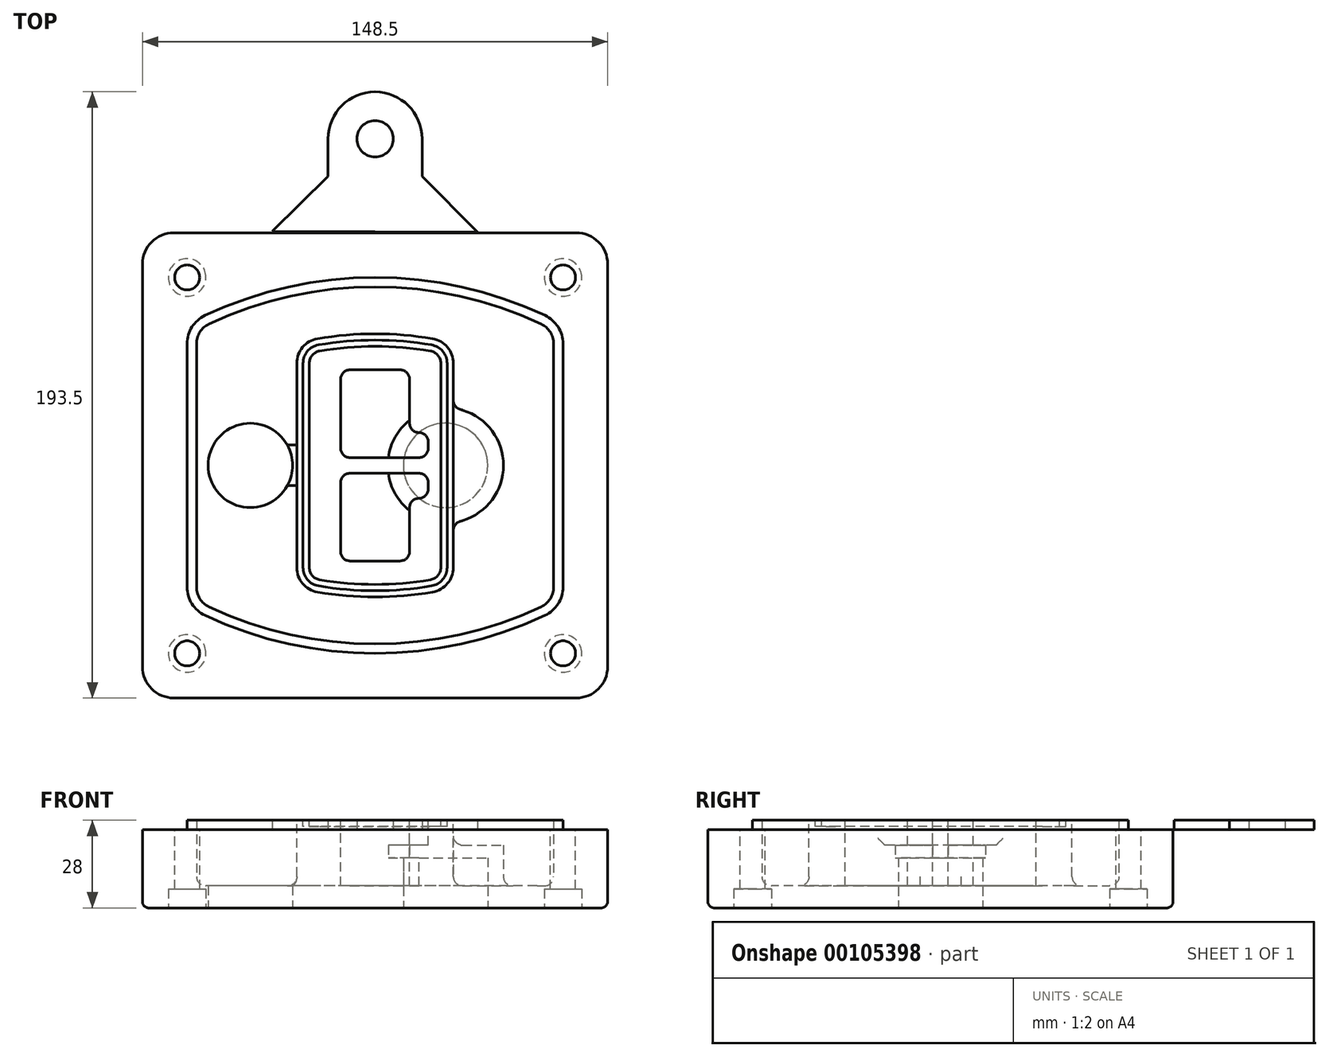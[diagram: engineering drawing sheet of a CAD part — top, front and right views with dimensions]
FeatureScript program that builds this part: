
annotation { "Feature Type Name" : "Feature", "Feature Type Description" : "" }
export const myFeature = defineFeature(function(context is Context, id is Id, definition is map)
    precondition{}
    {
        {
            var Q0;
            Q0=qCreatedBy(makeId("Top.planeOp"),FACE);
            var sketch = newSketch(context, id + "F0", { "sketchPlane" : qUnion([Q0])});
            skPoint(sketch, "E0.rect.middle", {"position": v(0, 0) * mm});
            skLineSegment(sketch, "E1.bottom", {"start": v(-64.25, -74.25) * mm, "end": v(64.25, -74.25) * mm});
            skLineSegment(sketch, "E1.top", {"start": v(-64.25, 74.25) * mm, "end": v(64.25, 74.25) * mm});
            skLineSegment(sketch, "E1.left", {"start": v(-74.25, -64.25) * mm, "end": v(-74.25, 64.25) * mm});
            skLineSegment(sketch, "E1.right", {"start": v(74.25, -64.25) * mm, "end": v(74.25, 64.25) * mm});
            skLineSegment(sketch, "E2", {"start": v(-74.25, 74.25) * mm, "end": v(74.25, -74.25) * mm, "construction": true});
            skLineSegment(sketch, "E3", {"start": v(74.25, 74.25) * mm, "end": v(-74.25, -74.25) * mm, "construction": true});
            skCircle(sketch, "E4", {"center": v(-60, 60) * mm, "radius": 4 * mm});
            skCircle(sketch, "E5", {"center": v(60, 60) * mm, "radius": 4 * mm});
            skCircle(sketch, "E6", {"center": v(60, -60) * mm, "radius": 4 * mm});
            skCircle(sketch, "E7", {"center": v(-60, -60) * mm, "radius": 4 * mm});
            skLineSegment(sketch, "E8", {"start": v(-60, 60) * mm, "end": v(60, 60) * mm, "construction": true});
            skLineSegment(sketch, "E9", {"start": v(60, 60) * mm, "end": v(60, -60) * mm, "construction": true});
            skLineSegment(sketch, "E10", {"start": v(60, -60) * mm, "end": v(-60, -60) * mm, "construction": true});
            skLineSegment(sketch, "E11", {"start": v(-60, -60) * mm, "end": v(-60, 60) * mm, "construction": true});
            skLineSegment(sketch, "E12", {"start": v(-60, 38.83) * mm, "end": v(-60, -38.83) * mm});
            skLineSegment(sketch, "E13", {"start": v(60, 38.83) * mm, "end": v(60, -38.83) * mm});
            skArc(sketch, "E14", {"start": v(54.26, 47.88) * mm, "mid": v(0, 60) * mm, "end": v(-54.26, 47.88) * mm});
            skArc(sketch, "E15", {"start": v(-54.26, -47.88) * mm, "mid": v(0, -60) * mm, "end": v(54.26, -47.88) * mm});
            skLineSegment(sketch, "E16", {"start": v(-60, 0) * mm, "end": v(60, 0) * mm, "construction": true});
            skPoint(sketch, "E17.visualSharp", {"position": v(-60, -45) * mm});
            skArc(sketch, "E17.filletArc", {"start": v(-60, -38.83) * mm, "mid": v(-58.44, -44.2) * mm, "end": v(-54.26, -47.88) * mm});
            skPoint(sketch, "E18.visualSharp", {"position": v(-60, 45) * mm});
            skArc(sketch, "E18.filletArc", {"start": v(-54.26, 47.88) * mm, "mid": v(-58.44, 44.2) * mm, "end": v(-60, 38.83) * mm});
            skPoint(sketch, "E19.visualSharp", {"position": v(60, 45) * mm});
            skArc(sketch, "E19.filletArc", {"start": v(60, 38.83) * mm, "mid": v(58.44, 44.2) * mm, "end": v(54.26, 47.88) * mm});
            skPoint(sketch, "E20.visualSharp", {"position": v(60, -45) * mm});
            skArc(sketch, "E20.filletArc", {"start": v(54.26, -47.88) * mm, "mid": v(58.44, -44.2) * mm, "end": v(60, -38.83) * mm});
            skPoint(sketch, "E21.visualSharp", {"position": v(-74.25, 74.25) * mm});
            skArc(sketch, "E21.filletArc", {"start": v(-64.25, 74.25) * mm, "mid": v(-71.32, 71.32) * mm, "end": v(-74.25, 64.25) * mm});
            skPoint(sketch, "E22.visualSharp", {"position": v(74.25, 74.25) * mm});
            skArc(sketch, "E22.filletArc", {"start": v(74.25, 64.25) * mm, "mid": v(71.32, 71.32) * mm, "end": v(64.25, 74.25) * mm});
            skPoint(sketch, "E23.visualSharp", {"position": v(74.25, -74.25) * mm});
            skArc(sketch, "E23.filletArc", {"start": v(64.25, -74.25) * mm, "mid": v(71.32, -71.32) * mm, "end": v(74.25, -64.25) * mm});
            skPoint(sketch, "E24.visualSharp", {"position": v(-74.25, -74.25) * mm});
            skArc(sketch, "E24.filletArc", {"start": v(-74.25, -64.25) * mm, "mid": v(-71.32, -71.32) * mm, "end": v(-64.25, -74.25) * mm});
            skArc(sketch, "E25.0", {"start": v(57, 38.83) * mm, "mid": v(55.9, 42.58) * mm, "end": v(52.98, 45.17) * mm});
            skLineSegment(sketch, "E25.1", {"start": v(57, 38.83) * mm, "end": v(57, -38.83) * mm});
            skArc(sketch, "E25.2", {"start": v(52.98, -45.17) * mm, "mid": v(55.9, -42.58) * mm, "end": v(57, -38.83) * mm});
            skArc(sketch, "E25.3", {"start": v(-52.98, -45.17) * mm, "mid": v(0, -57) * mm, "end": v(52.98, -45.17) * mm});
            skArc(sketch, "E25.4", {"start": v(-57, -38.83) * mm, "mid": v(-55.9, -42.58) * mm, "end": v(-52.98, -45.17) * mm});
            skArc(sketch, "E25.5", {"start": v(52.98, 45.17) * mm, "mid": v(0, 57) * mm, "end": v(-52.98, 45.17) * mm});
            skLineSegment(sketch, "E25.6", {"start": v(-57, 38.83) * mm, "end": v(-57, -38.83) * mm});
            skArc(sketch, "E25.7", {"start": v(-52.98, 45.17) * mm, "mid": v(-55.9, 42.58) * mm, "end": v(-57, 38.83) * mm});
            skArc(sketch, "E26.0", {"start": v(-55.96, 51.5) * mm, "mid": v(-61.82, 46.33) * mm, "end": v(-64, 38.83) * mm});
            skArc(sketch, "E26.1", {"start": v(55.96, 51.5) * mm, "mid": v(0, 64) * mm, "end": v(-55.96, 51.5) * mm});
            skArc(sketch, "E26.2", {"start": v(64, 38.83) * mm, "mid": v(61.82, 46.33) * mm, "end": v(55.96, 51.5) * mm});
            skLineSegment(sketch, "E26.3", {"start": v(64, 38.83) * mm, "end": v(64, -38.83) * mm});
            skArc(sketch, "E26.4", {"start": v(55.96, -51.5) * mm, "mid": v(61.82, -46.33) * mm, "end": v(64, -38.83) * mm});
            skLineSegment(sketch, "E26.5", {"start": v(-64, 38.83) * mm, "end": v(-64, -38.83) * mm});
            skArc(sketch, "E26.6", {"start": v(-55.96, -51.5) * mm, "mid": v(0, -64) * mm, "end": v(55.96, -51.5) * mm});
            skArc(sketch, "E26.7", {"start": v(-64, -38.83) * mm, "mid": v(-61.82, -46.33) * mm, "end": v(-55.96, -51.5) * mm});
            skSolve(sketch);
        }
        {
            var Q0;
            Q0=makeQuery(id+"F0.imprint","IMPRINT",FACE,{"disambiguationData":[TD([[makeQuery(id+"F0.imprint","IMPRINT",EDGE,{"derivedFrom":sQuery(id+"F0.wireOp",EDGE,"E1.bottom")}),1.0]])]});
            var Q1;
            Q1=makeQuery(id+"F0.imprint","IMPRINT",FACE,{"disambiguationData":[TD([[makeQuery(id+"F0.imprint","IMPRINT",EDGE,{"derivedFrom":sQuery(id+"F0.wireOp",EDGE,"E12")}),1.0]])]});
            var Q2;
            Q2=makeQuery(id+"F0.imprint","IMPRINT",FACE,{"disambiguationData":[TD([[makeQuery(id+"F0.imprint","IMPRINT",EDGE,{"derivedFrom":sQuery(id+"F0.wireOp",EDGE,"E25.0")}),1.0]])]});
            var Q3;
            Q3=makeQuery(id+"F0.imprint","IMPRINT",FACE,{"disambiguationData":[TD([[makeQuery(id+"F0.imprint","IMPRINT",EDGE,{"derivedFrom":sQuery(id+"F0.wireOp",EDGE,"E12")}),-1.0]])]});
            extrude(context, id + "F1", {"entities" : qUnion([Q0, Q1, Q2, Q3]), "oppositeDirection" : true, "depth" : 25 * mm});
        }
        {
            var Q0;
            Q0=makeQuery(id+"F0.imprint","IMPRINT",FACE,{"disambiguationData":[TD([[makeQuery(id+"F0.imprint","IMPRINT",EDGE,{"derivedFrom":sQuery(id+"F0.wireOp",EDGE,"E12")}),1.0]])]});
            extrude(context, id + "F2", {"entities" : qUnion([Q0]), "operationType" : NewBodyOperationType.ADD, "depth" : 3 * mm});
        }
        {
            var Q0;
            Q0=makeQuery(id+"F0.imprint","IMPRINT",FACE,{"disambiguationData":[TD([[makeQuery(id+"F0.imprint","IMPRINT",EDGE,{"derivedFrom":sQuery(id+"F0.wireOp",EDGE,"E25.0")}),1.0]])]});
            extrude(context, id + "F3", {"entities" : qUnion([Q0]), "operationType" : NewBodyOperationType.REMOVE, "oppositeDirection" : true, "depth" : 18 * mm});
        }
        {
            var Q0;
            Q0=makeQuery(id+"F2.opExtrude","CAP_FACE",FACE,{"disambiguationData":[OSD([sQuery(id+"F0.wireOp",EDGE,"E12"),sQuery(id+"F0.wireOp",EDGE,"E13"),sQuery(id+"F0.wireOp",EDGE,"E14"),sQuery(id+"F0.wireOp",EDGE,"E15"),sQuery(id+"F0.wireOp",EDGE,"E17.filletArc"),sQuery(id+"F0.wireOp",EDGE,"E18.filletArc"),sQuery(id+"F0.wireOp",EDGE,"E19.filletArc"),sQuery(id+"F0.wireOp",EDGE,"E20.filletArc"),sQuery(id+"F0.wireOp",EDGE,"E25.0"),sQuery(id+"F0.wireOp",EDGE,"E25.1"),sQuery(id+"F0.wireOp",EDGE,"E25.2"),sQuery(id+"F0.wireOp",EDGE,"E25.3"),sQuery(id+"F0.wireOp",EDGE,"E25.4"),sQuery(id+"F0.wireOp",EDGE,"E25.5"),sQuery(id+"F0.wireOp",EDGE,"E25.6"),sQuery(id+"F0.wireOp",EDGE,"E25.7")])],"isStart":false});
            var sketch = newSketch(context, id + "F4", { "sketchPlane" : qUnion([Q0])});
            skArc(sketch, "E27.0", {"start": v(-18.34, -40.45) * mm, "mid": v(0, -42) * mm, "end": v(18.34, -40.45) * mm});
            skArc(sketch, "E28.0", {"start": v(18.34, 40.45) * mm, "mid": v(0, 42) * mm, "end": v(-18.34, 40.45) * mm});
            skLineSegment(sketch, "E29", {"start": v(-25, 32.57) * mm, "end": v(-25, -32.57) * mm});
            skLineSegment(sketch, "E30", {"start": v(25, 32.57) * mm, "end": v(25, -32.57) * mm});
            skLineSegment(sketch, "E31", {"start": v(-25, 39.1) * mm, "end": v(25, 39.1) * mm, "construction": true});
            skLineSegment(sketch, "E32", {"start": v(-25, -39.1) * mm, "end": v(25, -39.1) * mm, "construction": true});
            skPoint(sketch, "E33.visualSharp", {"position": v(-25, 39.1) * mm});
            skArc(sketch, "E33.filletArc", {"start": v(-18.34, 40.45) * mm, "mid": v(-23.11, 37.73) * mm, "end": v(-25, 32.57) * mm});
            skPoint(sketch, "E34.visualSharp", {"position": v(25, 39.1) * mm});
            skArc(sketch, "E34.filletArc", {"start": v(25, 32.57) * mm, "mid": v(23.11, 37.73) * mm, "end": v(18.34, 40.45) * mm});
            skPoint(sketch, "E35.visualSharp", {"position": v(25, -39.1) * mm});
            skArc(sketch, "E35.filletArc", {"start": v(18.34, -40.45) * mm, "mid": v(23.11, -37.73) * mm, "end": v(25, -32.57) * mm});
            skPoint(sketch, "E36.visualSharp", {"position": v(-25, -39.1) * mm});
            skArc(sketch, "E36.filletArc", {"start": v(-25, -32.57) * mm, "mid": v(-23.11, -37.73) * mm, "end": v(-18.34, -40.45) * mm});
            skArc(sketch, "E37.0", {"start": v(52.98, 45.17) * mm, "mid": v(0, 57) * mm, "end": v(-52.98, 45.17) * mm});
            skArc(sketch, "E37.1", {"start": v(-52.98, 45.17) * mm, "mid": v(-55.9, 42.58) * mm, "end": v(-57, 38.83) * mm});
            skLineSegment(sketch, "E37.2", {"start": v(-57, 38.83) * mm, "end": v(-57, -38.83) * mm});
            skArc(sketch, "E37.3", {"start": v(-57, -38.83) * mm, "mid": v(-55.9, -42.58) * mm, "end": v(-52.98, -45.17) * mm});
            skArc(sketch, "E37.4", {"start": v(-52.98, -45.17) * mm, "mid": v(0, -57) * mm, "end": v(52.98, -45.17) * mm});
            skArc(sketch, "E37.5", {"start": v(52.98, -45.17) * mm, "mid": v(55.9, -42.58) * mm, "end": v(57, -38.83) * mm});
            skLineSegment(sketch, "E37.6", {"start": v(57, 38.83) * mm, "end": v(57, -38.83) * mm});
            skArc(sketch, "E37.7", {"start": v(57, 38.83) * mm, "mid": v(55.9, 42.58) * mm, "end": v(52.98, 45.17) * mm});
            skLineSegment(sketch, "E38.0", {"start": v(23, 32.57) * mm, "end": v(23, -32.57) * mm});
            skArc(sketch, "E38.1", {"start": v(18, -38.48) * mm, "mid": v(21.58, -36.44) * mm, "end": v(23, -32.57) * mm});
            skArc(sketch, "E38.2", {"start": v(-18, -38.48) * mm, "mid": v(0, -40) * mm, "end": v(18, -38.48) * mm});
            skArc(sketch, "E38.3", {"start": v(-23, -32.57) * mm, "mid": v(-21.58, -36.44) * mm, "end": v(-18, -38.48) * mm});
            skLineSegment(sketch, "E38.4", {"start": v(-23, 32.57) * mm, "end": v(-23, -32.57) * mm});
            skArc(sketch, "E38.5", {"start": v(23, 32.57) * mm, "mid": v(21.58, 36.44) * mm, "end": v(18, 38.48) * mm});
            skArc(sketch, "E38.6", {"start": v(-18, 38.48) * mm, "mid": v(-21.58, 36.44) * mm, "end": v(-23, 32.57) * mm});
            skArc(sketch, "E38.7", {"start": v(18, 38.48) * mm, "mid": v(0, 40) * mm, "end": v(-18, 38.48) * mm});
            skArc(sketch, "E39.0", {"start": v(21, 32.57) * mm, "mid": v(20.06, 35.15) * mm, "end": v(17.67, 36.5) * mm});
            skLineSegment(sketch, "E39.1", {"start": v(21, 32.57) * mm, "end": v(21, -32.57) * mm});
            skArc(sketch, "E39.2", {"start": v(17.67, -36.5) * mm, "mid": v(20.06, -35.15) * mm, "end": v(21, -32.57) * mm});
            skArc(sketch, "E39.3", {"start": v(-17.67, -36.5) * mm, "mid": v(0, -38) * mm, "end": v(17.67, -36.5) * mm});
            skArc(sketch, "E39.4", {"start": v(-21, -32.57) * mm, "mid": v(-20.06, -35.15) * mm, "end": v(-17.67, -36.5) * mm});
            skArc(sketch, "E39.5", {"start": v(17.67, 36.5) * mm, "mid": v(0, 38) * mm, "end": v(-17.67, 36.5) * mm});
            skLineSegment(sketch, "E39.6", {"start": v(-21, 32.57) * mm, "end": v(-21, -32.57) * mm});
            skArc(sketch, "E39.7", {"start": v(-17.67, 36.5) * mm, "mid": v(-20.06, 35.15) * mm, "end": v(-21, 32.57) * mm});
            skLineSegment(sketch, "E40", {"start": v(-25, 0) * mm, "end": v(25, 0) * mm, "construction": true});
            skLineSegment(sketch, "E41", {"start": v(-11, 5.5) * mm, "end": v(-11, 27.5) * mm});
            skLineSegment(sketch, "E42", {"start": v(-8, 30.5) * mm, "end": v(8, 30.5) * mm});
            skLineSegment(sketch, "E43", {"start": v(11, 27.5) * mm, "end": v(11, 13.5) * mm});
            skLineSegment(sketch, "E44", {"start": v(14, 10.5) * mm, "end": v(14, 10.5) * mm});
            skLineSegment(sketch, "E45", {"start": v(17, 7.5) * mm, "end": v(17, 5.5) * mm});
            skLineSegment(sketch, "E46", {"start": v(14, 2.5) * mm, "end": v(-8, 2.5) * mm});
            skPoint(sketch, "E47.visualSharp", {"position": v(-11, 30.5) * mm});
            skArc(sketch, "E47.filletArc", {"start": v(-8, 30.5) * mm, "mid": v(-10.12, 29.62) * mm, "end": v(-11, 27.5) * mm});
            skPoint(sketch, "E48.visualSharp", {"position": v(11, 30.5) * mm});
            skArc(sketch, "E48.filletArc", {"start": v(11, 27.5) * mm, "mid": v(10.12, 29.62) * mm, "end": v(8, 30.5) * mm});
            skPoint(sketch, "E49.visualSharp", {"position": v(11, 10.5) * mm});
            skArc(sketch, "E49.filletArc", {"start": v(11, 13.5) * mm, "mid": v(11.88, 11.38) * mm, "end": v(14, 10.5) * mm});
            skPoint(sketch, "E50.visualSharp", {"position": v(17, 10.5) * mm});
            skArc(sketch, "E50.filletArc", {"start": v(17, 7.5) * mm, "mid": v(16.12, 9.62) * mm, "end": v(14, 10.5) * mm});
            skPoint(sketch, "E51.visualSharp", {"position": v(17, 2.5) * mm});
            skArc(sketch, "E51.filletArc", {"start": v(14, 2.5) * mm, "mid": v(16.12, 3.38) * mm, "end": v(17, 5.5) * mm});
            skPoint(sketch, "E52.visualSharp", {"position": v(-11, 2.5) * mm});
            skArc(sketch, "E52.filletArc", {"start": v(-11, 5.5) * mm, "mid": v(-10.12, 3.38) * mm, "end": v(-8, 2.5) * mm});
            skLineSegment(sketch, "E53.0.MirrorCS", {"start": v(14, -2.5) * mm, "end": v(-8, -2.5) * mm});
            skArc(sketch, "E54.0.MirrorCS", {"start": v(-11, -5.5) * mm, "mid": v(-10.12, -3.38) * mm, "end": v(-8, -2.5) * mm});
            skLineSegment(sketch, "E55.0.MirrorCS", {"start": v(-11, -5.5) * mm, "end": v(-11, -27.5) * mm});
            skArc(sketch, "E56.0.MirrorCS", {"start": v(-8, -30.5) * mm, "mid": v(-10.12, -29.62) * mm, "end": v(-11, -27.5) * mm});
            skLineSegment(sketch, "E57.0.MirrorCS", {"start": v(-8, -30.5) * mm, "end": v(8, -30.5) * mm});
            skArc(sketch, "E58.0.MirrorCS", {"start": v(11, -27.5) * mm, "mid": v(10.12, -29.62) * mm, "end": v(8, -30.5) * mm});
            skLineSegment(sketch, "E59.0.MirrorCS", {"start": v(11, -27.5) * mm, "end": v(11, -13.5) * mm});
            skArc(sketch, "E60.0.MirrorCS", {"start": v(11, -13.5) * mm, "mid": v(11.88, -11.38) * mm, "end": v(14, -10.5) * mm});
            skArc(sketch, "E61.0.MirrorCS", {"start": v(17, -7.5) * mm, "mid": v(16.12, -9.62) * mm, "end": v(14, -10.5) * mm});
            skLineSegment(sketch, "E62.0.MirrorCS", {"start": v(17, -7.5) * mm, "end": v(17, -5.5) * mm});
            skArc(sketch, "E63.0.MirrorCS", {"start": v(14, -2.5) * mm, "mid": v(16.12, -3.38) * mm, "end": v(17, -5.5) * mm});
            skSolve(sketch);
        }
        {
            var Q0;
            Q0=makeQuery(id+"F4.imprint","IMPRINT",FACE,{"disambiguationData":[TD([[makeQuery(id+"F4.imprint","IMPRINT",EDGE,{"derivedFrom":sQuery(id+"F4.wireOp",EDGE,"E27.0")}),1.0]])]});
            var Q1;
            Q1=makeQuery(id+"F4.imprint","IMPRINT",FACE,{"disambiguationData":[TD([[makeQuery(id+"F4.imprint","IMPRINT",EDGE,{"derivedFrom":sQuery(id+"F4.wireOp",EDGE,"E38.0")}),-1.0]])]});
            var Q2;
            Q2=makeQuery(id+"F4.imprint","IMPRINT",FACE,{"disambiguationData":[TD([[makeQuery(id+"F4.imprint","IMPRINT",EDGE,{"derivedFrom":sQuery(id+"F4.wireOp",EDGE,"E39.0")}),1.0]])]});
            extrude(context, id + "F5", {"entities" : qUnion([Q0, Q1, Q2]), "operationType" : NewBodyOperationType.ADD, "endBound" : BoundingType.UP_TO_NEXT, "oppositeDirection" : true, "depth" : 25 * mm});
        }
        {
            var Q0;
            Q0=makeQuery(id+"F4.imprint","IMPRINT",FACE,{"disambiguationData":[TD([[makeQuery(id+"F4.imprint","IMPRINT",EDGE,{"derivedFrom":sQuery(id+"F4.wireOp",EDGE,"E38.0")}),-1.0]])]});
            extrude(context, id + "F6", {"entities" : qUnion([Q0]), "operationType" : NewBodyOperationType.REMOVE, "oppositeDirection" : true, "depth" : 2 * mm});
        }
        {
            var Q0;
            Q0=makeQuery(id+"F1.opExtrude","CAP_FACE",FACE,{"disambiguationData":[OSD([sQuery(id+"F0.wireOp",EDGE,"E1.bottom"),sQuery(id+"F0.wireOp",EDGE,"E1.top"),sQuery(id+"F0.wireOp",EDGE,"E1.left"),sQuery(id+"F0.wireOp",EDGE,"E1.right"),sQuery(id+"F0.wireOp",EDGE,"E4"),sQuery(id+"F0.wireOp",EDGE,"E5"),sQuery(id+"F0.wireOp",EDGE,"E6"),sQuery(id+"F0.wireOp",EDGE,"E7"),sQuery(id+"F0.wireOp",EDGE,"E21.filletArc"),sQuery(id+"F0.wireOp",EDGE,"E22.filletArc"),sQuery(id+"F0.wireOp",EDGE,"E23.filletArc"),sQuery(id+"F0.wireOp",EDGE,"E24.filletArc")])],"isStart":false});
            var sketch = newSketch(context, id + "F7", { "sketchPlane" : qUnion([Q0])});
            skCircle(sketch, "E64", {"center": v(22.5, 0) * mm, "radius": 13.47 * mm});
            skCircle(sketch, "E65", {"center": v(-39.81, 0) * mm, "radius": 13.47 * mm});
            skLineSegment(sketch, "E66", {"start": v(74.25, 0) * mm, "end": v(-74.25, 0) * mm});
            skCircle(sketch, "E67", {"center": v(22.5, 0) * mm, "radius": 18.47 * mm});
            skCircle(sketch, "E68", {"center": v(60, -60) * mm, "radius": 6 * mm});
            skCircle(sketch, "E69", {"center": v(-60, -60) * mm, "radius": 6 * mm});
            skCircle(sketch, "E70", {"center": v(-60, 60) * mm, "radius": 6 * mm});
            skCircle(sketch, "E71", {"center": v(60, 60) * mm, "radius": 6 * mm});
            skSolve(sketch);
        }
        {
            var Q0;
            {var subQ1=sQuery(id+"F7.wireOp",EDGE,"E66");var subQ4=sQuery(id+"F7.wireOp",EDGE,"E64");var subQ6=makeQuery(id+"F7.imprint","INTERSECT",VERTEX,{"disambiguationData":[OD(0.0)],"derivedFrom":[subQ4,subQ1]});Q0=makeQuery(id+"F7.imprint","IMPRINT",FACE,{"disambiguationData":[TD([[makeQuery(id+"F7.imprint","IMPRINT",EDGE,{"disambiguationData":[TD([[subQ6,-1.0]])],"derivedFrom":subQ4}),-1.0]])]});}
            var Q1;
            {var subQ0=sQuery(id+"F7.wireOp",EDGE,"E66");var subQ1=sQuery(id+"F7.wireOp",EDGE,"E64");var subQ3=makeQuery(id+"F7.imprint","INTERSECT",VERTEX,{"disambiguationData":[OD(0.0)],"derivedFrom":[subQ1,subQ0]});Q1=makeQuery(id+"F7.imprint","IMPRINT",FACE,{"disambiguationData":[TD([[makeQuery(id+"F7.imprint","IMPRINT",EDGE,{"disambiguationData":[TD([[subQ3,-1.0]])],"derivedFrom":subQ1}),1.0]])]});}
            var Q2;
            {var subQ0=sQuery(id+"F7.wireOp",EDGE,"E66");var subQ1=sQuery(id+"F7.wireOp",EDGE,"E64");var subQ3=makeQuery(id+"F7.imprint","INTERSECT",VERTEX,{"disambiguationData":[OD(0.0)],"derivedFrom":[subQ1,subQ0]});Q2=makeQuery(id+"F7.imprint","IMPRINT",FACE,{"disambiguationData":[TD([[makeQuery(id+"F7.imprint","IMPRINT",EDGE,{"disambiguationData":[TD([[subQ3,1.0]])],"derivedFrom":subQ1}),1.0]])]});}
            var Q3;
            {var subQ1=sQuery(id+"F7.wireOp",EDGE,"E66");var subQ4=sQuery(id+"F7.wireOp",EDGE,"E64");var subQ6=makeQuery(id+"F7.imprint","INTERSECT",VERTEX,{"disambiguationData":[OD(0.0)],"derivedFrom":[subQ4,subQ1]});Q3=makeQuery(id+"F7.imprint","IMPRINT",FACE,{"disambiguationData":[TD([[makeQuery(id+"F7.imprint","IMPRINT",EDGE,{"disambiguationData":[TD([[subQ6,1.0]])],"derivedFrom":subQ4}),-1.0]])]});}
            extrude(context, id + "F8", {"entities" : qUnion([Q0, Q1, Q2, Q3]), "operationType" : NewBodyOperationType.ADD, "oppositeDirection" : true, "depth" : 20 * mm});
        }
        {
            var Q0;
            {var subQ0=sQuery(id+"F7.wireOp",EDGE,"E66");var subQ1=sQuery(id+"F7.wireOp",EDGE,"E64");var subQ3=makeQuery(id+"F7.imprint","INTERSECT",VERTEX,{"disambiguationData":[OD(0.0)],"derivedFrom":[subQ1,subQ0]});Q0=makeQuery(id+"F7.imprint","IMPRINT",FACE,{"disambiguationData":[TD([[makeQuery(id+"F7.imprint","IMPRINT",EDGE,{"disambiguationData":[TD([[subQ3,-1.0]])],"derivedFrom":subQ1}),1.0]])]});}
            var Q1;
            {var subQ0=sQuery(id+"F7.wireOp",EDGE,"E66");var subQ1=sQuery(id+"F7.wireOp",EDGE,"E64");var subQ3=makeQuery(id+"F7.imprint","INTERSECT",VERTEX,{"disambiguationData":[OD(0.0)],"derivedFrom":[subQ1,subQ0]});Q1=makeQuery(id+"F7.imprint","IMPRINT",FACE,{"disambiguationData":[TD([[makeQuery(id+"F7.imprint","IMPRINT",EDGE,{"disambiguationData":[TD([[subQ3,1.0]])],"derivedFrom":subQ1}),1.0]])]});}
            extrude(context, id + "F9", {"entities" : qUnion([Q0, Q1]), "operationType" : NewBodyOperationType.REMOVE, "oppositeDirection" : true, "depth" : 16 * mm});
        }
        {
            var Q0;
            {var subQ0=sQuery(id+"F7.wireOp",EDGE,"E66");var subQ1=sQuery(id+"F7.wireOp",EDGE,"E65");var subQ3=makeQuery(id+"F7.imprint","INTERSECT",VERTEX,{"disambiguationData":[OD(0.0)],"derivedFrom":[subQ1,subQ0]});Q0=makeQuery(id+"F7.imprint","IMPRINT",FACE,{"disambiguationData":[TD([[makeQuery(id+"F7.imprint","IMPRINT",EDGE,{"disambiguationData":[TD([[subQ3,-1.0]])],"derivedFrom":subQ1}),1.0]])]});}
            var Q1;
            {var subQ0=sQuery(id+"F7.wireOp",EDGE,"E66");var subQ1=sQuery(id+"F7.wireOp",EDGE,"E65");var subQ3=makeQuery(id+"F7.imprint","INTERSECT",VERTEX,{"disambiguationData":[OD(0.0)],"derivedFrom":[subQ1,subQ0]});Q1=makeQuery(id+"F7.imprint","IMPRINT",FACE,{"disambiguationData":[TD([[makeQuery(id+"F7.imprint","IMPRINT",EDGE,{"disambiguationData":[TD([[subQ3,1.0]])],"derivedFrom":subQ1}),1.0]])]});}
            extrude(context, id + "F10", {"entities" : qUnion([Q0, Q1]), "operationType" : NewBodyOperationType.REMOVE, "oppositeDirection" : true, "depth" : 25 * mm});
        }
        {
            var Q0;
            Q0=makeQuery(id+"F7.imprint","IMPRINT",FACE,{"disambiguationData":[TD([[makeQuery(id+"F7.imprint","IMPRINT",EDGE,{"derivedFrom":sQuery(id+"F7.wireOp",EDGE,"E68")}),1.0]])]});
            var Q1;
            Q1=makeQuery(id+"F7.imprint","IMPRINT",FACE,{"disambiguationData":[TD([[makeQuery(id+"F7.imprint","IMPRINT",EDGE,{"derivedFrom":makeQuery(id+"F1.opExtrude","CAP_EDGE",EDGE,{"disambiguationData":[OSD([sQuery(id+"F0.wireOp",EDGE,"E5")])],"isStart":false})}),-1.0]])]});
            var Q2;
            Q2=makeQuery(id+"F7.imprint","IMPRINT",FACE,{"disambiguationData":[TD([[makeQuery(id+"F7.imprint","IMPRINT",EDGE,{"derivedFrom":sQuery(id+"F7.wireOp",EDGE,"E69")}),1.0]])]});
            var Q3;
            Q3=makeQuery(id+"F7.imprint","IMPRINT",FACE,{"disambiguationData":[TD([[makeQuery(id+"F7.imprint","IMPRINT",EDGE,{"derivedFrom":makeQuery(id+"F1.opExtrude","CAP_EDGE",EDGE,{"disambiguationData":[OSD([sQuery(id+"F0.wireOp",EDGE,"E4")])],"isStart":false})}),-1.0]])]});
            var Q4;
            Q4=makeQuery(id+"F7.imprint","IMPRINT",FACE,{"disambiguationData":[TD([[makeQuery(id+"F7.imprint","IMPRINT",EDGE,{"derivedFrom":sQuery(id+"F7.wireOp",EDGE,"E70")}),1.0]])]});
            var Q5;
            Q5=makeQuery(id+"F7.imprint","IMPRINT",FACE,{"disambiguationData":[TD([[makeQuery(id+"F7.imprint","IMPRINT",EDGE,{"derivedFrom":makeQuery(id+"F1.opExtrude","CAP_EDGE",EDGE,{"disambiguationData":[OSD([sQuery(id+"F0.wireOp",EDGE,"E7")])],"isStart":false})}),-1.0]])]});
            var Q6;
            Q6=makeQuery(id+"F7.imprint","IMPRINT",FACE,{"disambiguationData":[TD([[makeQuery(id+"F7.imprint","IMPRINT",EDGE,{"derivedFrom":sQuery(id+"F7.wireOp",EDGE,"E71")}),1.0]])]});
            var Q7;
            Q7=makeQuery(id+"F7.imprint","IMPRINT",FACE,{"disambiguationData":[TD([[makeQuery(id+"F7.imprint","IMPRINT",EDGE,{"derivedFrom":makeQuery(id+"F1.opExtrude","CAP_EDGE",EDGE,{"disambiguationData":[OSD([sQuery(id+"F0.wireOp",EDGE,"E6")])],"isStart":false})}),-1.0]])]});
            extrude(context, id + "F11", {"entities" : qUnion([Q0, Q1, Q2, Q3, Q4, Q5, Q6, Q7]), "operationType" : NewBodyOperationType.REMOVE, "oppositeDirection" : true, "depth" : 6 * mm});
        }
        {
            var Q0;
            Q0=makeQuery(id+"F9.boolean.opBoolean","COPY",FACE,{"derivedFrom":makeQuery(id+"F9.opExtrude","CAP_FACE",FACE,{"disambiguationData":[OSD([sQuery(id+"F7.wireOp",EDGE,"E64")])],"isStart":false})});
            var sketch = newSketch(context, id + "F12", { "sketchPlane" : qUnion([Q0])});
            skArc(sketch, "E72.0", {"start": v(11, 14.45) * mm, "mid": v(6.45, 9.13) * mm, "end": v(4.2, 2.5) * mm});
            skArc(sketch, "E72.1", {"start": v(4.2, -2.5) * mm, "mid": v(6.45, -9.13) * mm, "end": v(11, -14.45) * mm});
            skLineSegment(sketch, "E73", {"start": v(4.2, -2.5) * mm, "end": v(14, -2.5) * mm});
            skLineSegment(sketch, "E74.0", {"start": v(14, 2.5) * mm, "end": v(4.2, 2.5) * mm});
            skArc(sketch, "E74.1", {"start": v(14, 2.5) * mm, "mid": v(16.12, 3.38) * mm, "end": v(17, 5.5) * mm});
            skLineSegment(sketch, "E74.2", {"start": v(17, 7.5) * mm, "end": v(17, 5.5) * mm});
            skArc(sketch, "E74.3", {"start": v(17, 7.5) * mm, "mid": v(16.12, 9.62) * mm, "end": v(14, 10.5) * mm});
            skArc(sketch, "E74.4", {"start": v(11, 13.5) * mm, "mid": v(11.88, 11.38) * mm, "end": v(14, 10.5) * mm});
            skLineSegment(sketch, "E74.5", {"start": v(11, 14.45) * mm, "end": v(11, 13.5) * mm});
            skLineSegment(sketch, "E74.7", {"start": v(14, -2.5) * mm, "end": v(4.2, -2.5) * mm});
            skArc(sketch, "E74.8", {"start": v(14, -2.5) * mm, "mid": v(16.12, -3.38) * mm, "end": v(17, -5.5) * mm});
            skLineSegment(sketch, "E74.9", {"start": v(17, -7.5) * mm, "end": v(17, -5.5) * mm});
            skArc(sketch, "E74.10", {"start": v(17, -7.5) * mm, "mid": v(16.12, -9.62) * mm, "end": v(14, -10.5) * mm});
            skArc(sketch, "E74.11", {"start": v(11, -13.5) * mm, "mid": v(11.88, -11.38) * mm, "end": v(14, -10.5) * mm});
            skLineSegment(sketch, "E74.12", {"start": v(11, -14.45) * mm, "end": v(11, -13.5) * mm});
            skPoint(sketch, "E75.orphan", {"position": v(11, -27.5) * mm});
            skPoint(sketch, "E76.orphan", {"position": v(-8, -2.5) * mm});
            skPoint(sketch, "E77.orphan", {"position": v(-8, 2.5) * mm});
            skPoint(sketch, "E78.orphan", {"position": v(11, 27.5) * mm});
            skSolve(sketch);
        }
        {
            var Q0;
            {var subQ7=sQuery(id+"F12.wireOp",EDGE,"E72.0");var subQ14=sQuery(id+"F12.wireOp",EDGE,"E72.1");var subQ16=sQuery(id+"F12.wireOp",EDGE,"E74.1");var subQ18=sQuery(id+"F12.wireOp",EDGE,"E74.8");Q0=qUnion([makeQuery(id+"F12.imprint","IMPRINT",FACE,{"disambiguationData":[TD([[makeQuery(id+"F12.imprint","IMPRINT",EDGE,{"derivedFrom":subQ7}),1.0]])]}),makeQuery(id+"F12.imprint","IMPRINT",FACE,{"disambiguationData":[TD([[makeQuery(id+"F12.imprint","IMPRINT",EDGE,{"derivedFrom":subQ14}),1.0]])]}),makeQuery(id+"F12.imprint","IMPRINT",FACE,{"disambiguationData":[TD([[makeQuery(id+"F12.imprint","IMPRINT",EDGE,{"derivedFrom":subQ16}),1.0]])]}),makeQuery(id+"F12.imprint","IMPRINT",FACE,{"disambiguationData":[TD([[makeQuery(id+"F12.imprint","IMPRINT",EDGE,{"derivedFrom":subQ18}),-1.0]])]})]);}
            var Q1;
            Q1=makeQuery(id+"F5.boolean.opBoolean","SPLIT",FACE,{"disambiguationData":[TD([makeQuery(id+"F5.opExtrude","SWEPT_FACE",FACE,{"disambiguationData":[OSD([sQuery(id+"F4.wireOp",EDGE,"E41")])]})])],"derivedFrom":makeQuery(id+"F3.boolean.opBoolean","COPY",FACE,{"derivedFrom":makeQuery(id+"F3.opExtrude","CAP_FACE",FACE,{"disambiguationData":[OSD([sQuery(id+"F0.wireOp",EDGE,"E25.0"),sQuery(id+"F0.wireOp",EDGE,"E25.1"),sQuery(id+"F0.wireOp",EDGE,"E25.2"),sQuery(id+"F0.wireOp",EDGE,"E25.3"),sQuery(id+"F0.wireOp",EDGE,"E25.4"),sQuery(id+"F0.wireOp",EDGE,"E25.5"),sQuery(id+"F0.wireOp",EDGE,"E25.6"),sQuery(id+"F0.wireOp",EDGE,"E25.7")])],"isStart":false})})});
            extrude(context, id + "F13", {"entities" : qUnion([Q0]), "operationType" : NewBodyOperationType.REMOVE, "endBound" : BoundingType.UP_TO_SURFACE, "endBoundEntityFace" : qUnion([Q1]), "depth" : 25 * mm});
        }
        {
            var Q0;
            Q0=makeQuery(id+"F3.boolean.opBoolean","COPY",EDGE,{"derivedFrom":makeQuery(id+"F3.opExtrude","CAP_EDGE",EDGE,{"disambiguationData":[OSD([sQuery(id+"F0.wireOp",EDGE,"E25.6")])],"isStart":false})});
            var Q1;
            Q1=makeQuery(id+"F8.boolean.opBoolean","INTERSECT",EDGE,{"derivedFrom":[makeQuery(id+"F5.opExtrude","SWEPT_FACE",FACE,{"disambiguationData":[OSD([sQuery(id+"F4.wireOp",EDGE,"E30")])]}),makeQuery(id+"F8.opExtrude","CAP_FACE",FACE,{"disambiguationData":[OSD([sQuery(id+"F7.wireOp",EDGE,"E67")])],"isStart":false})]});
            var Q2;
            Q2=makeQuery(id+"F8.boolean.opBoolean","INTERSECT",EDGE,{"disambiguationData":[OD(1.0)],"derivedFrom":[makeQuery(id+"F5.opExtrude","SWEPT_FACE",FACE,{"disambiguationData":[OSD([sQuery(id+"F4.wireOp",EDGE,"E30")])]}),makeQuery(id+"F8.opExtrude","SWEPT_FACE",FACE,{"disambiguationData":[OSD([sQuery(id+"F7.wireOp",EDGE,"E67")])]})]});
            var Q3;
            {var subQ0=sQuery(id+"F4.wireOp",EDGE,"E30");Q3=makeQuery(id+"F8.boolean.opBoolean","SPLIT",EDGE,{"disambiguationData":[TD([makeQuery(id+"F5.opExtrude","SWEPT_FACE",FACE,{"disambiguationData":[OSD([sQuery(id+"F4.wireOp",EDGE,"E35.filletArc")])]})])],"derivedFrom":makeQuery(id+"F5.opExtrude","CAP_EDGE",EDGE,{"disambiguationData":[OSD([subQ0])],"isStart":false})});}
            var Q4;
            {var subQ0=sQuery(id+"F0.wireOp",EDGE,"E25.7");var subQ1=sQuery(id+"F0.wireOp",EDGE,"E25.1");var subQ2=sQuery(id+"F0.wireOp",EDGE,"E25.6");var subQ3=sQuery(id+"F0.wireOp",EDGE,"E25.5");var subQ4=sQuery(id+"F0.wireOp",EDGE,"E25.4");var subQ5=sQuery(id+"F0.wireOp",EDGE,"E25.0");var subQ6=sQuery(id+"F0.wireOp",EDGE,"E25.2");var subQ7=sQuery(id+"F0.wireOp",EDGE,"E25.3");Q4=makeQuery(id+"F8.boolean.opBoolean","INTERSECT",EDGE,{"derivedFrom":[makeQuery(id+"F5.boolean.opBoolean","SPLIT",FACE,{"disambiguationData":[TD([makeQuery(id+"F2.opExtrude","SWEPT_FACE",FACE,{"disambiguationData":[OSD([subQ5])]})])],"derivedFrom":makeQuery(id+"F3.boolean.opBoolean","COPY",FACE,{"derivedFrom":makeQuery(id+"F3.opExtrude","CAP_FACE",FACE,{"disambiguationData":[OSD([subQ5,subQ1,subQ6,subQ7,subQ4,subQ3,subQ2,subQ0])],"isStart":false})})}),makeQuery(id+"F8.opExtrude","SWEPT_FACE",FACE,{"disambiguationData":[OSD([sQuery(id+"F7.wireOp",EDGE,"E67")])]})]});}
            var Q5;
            Q5=makeQuery(id+"F8.boolean.opBoolean","INTERSECT",EDGE,{"disambiguationData":[OD(0.0)],"derivedFrom":[makeQuery(id+"F5.opExtrude","SWEPT_FACE",FACE,{"disambiguationData":[OSD([sQuery(id+"F4.wireOp",EDGE,"E30")])]}),makeQuery(id+"F8.opExtrude","SWEPT_FACE",FACE,{"disambiguationData":[OSD([sQuery(id+"F7.wireOp",EDGE,"E67")])]})]});
            fillet(context, id + "F14", {"entities" : qUnion([Q0, Q1, Q2, Q3, Q4, Q5]), "radius" : 3 * mm, "tangentPropagation" : true, "allowEdgeOverflow" : false});
        }
        {
            var Q0;
            Q0=makeQuery(id+"F1.opExtrude","CAP_EDGE",EDGE,{"disambiguationData":[OSD([sQuery(id+"F0.wireOp",EDGE,"E1.bottom")])],"isStart":false});
            fillet(context, id + "F15", {"entities" : qUnion([Q0]), "radius" : 2 * mm, "tangentPropagation" : true, "allowEdgeOverflow" : false});
        }
        {
            var Q0;
            Q0=qCreatedBy(makeId("Top.planeOp"),FACE);
            var sketch = newSketch(context, id + "F16", { "sketchPlane" : qUnion([Q0])});
            skCircle(sketch, "E79", {"center": v(0, 104.25) * mm, "radius": 6 * mm, "construction": true});
            skArc(sketch, "E80", {"start": v(15, 104.25) * mm, "mid": v(0, 119.25) * mm, "end": v(-15, 104.25) * mm});
            skLineSegment(sketch, "E81", {"start": v(-32.88, 74.7) * mm, "end": v(-15, 92.25) * mm});
            skLineSegment(sketch, "E82", {"start": v(-15, 92.25) * mm, "end": v(-15, 104.25) * mm});
            skLineSegment(sketch, "E83", {"start": v(32.72, 74.53) * mm, "end": v(15, 92.25) * mm});
            skLineSegment(sketch, "E84", {"start": v(15, 92.25) * mm, "end": v(15, 104.25) * mm});
            skLineSegment(sketch, "E85", {"start": v(-32.88, 74.7) * mm, "end": v(32.72, 74.53) * mm});
            skLineSegment(sketch, "E86", {"start": v(0, 104.25) * mm, "end": v(0, 74.61) * mm, "construction": true});
            skArc(sketch, "E87.MirrorCS", {"start": v(15, -104.25) * mm, "mid": v(0, -119.25) * mm, "end": v(-15, -104.25) * mm});
            skLineSegment(sketch, "E88.MirrorCS", {"start": v(32.72, -74.53) * mm, "end": v(15, -92.25) * mm});
            skLineSegment(sketch, "E89.MirrorCS", {"start": v(-32.88, -74.7) * mm, "end": v(-15, -92.25) * mm});
            skLineSegment(sketch, "E90.MirrorCS", {"start": v(-15, -92.25) * mm, "end": v(-15, -104.25) * mm});
            skLineSegment(sketch, "E91.MirrorCS", {"start": v(15, -92.25) * mm, "end": v(15, -104.25) * mm});
            skCircle(sketch, "E92.MirrorC", {"center": v(0, -104.25) * mm, "radius": 6 * mm, "construction": true});
            skLineSegment(sketch, "E93.MirrorCS", {"start": v(0, -104.25) * mm, "end": v(0, -74.61) * mm, "construction": true});
            skLineSegment(sketch, "E94.MirrorCS", {"start": v(-32.88, -74.7) * mm, "end": v(32.72, -74.53) * mm});
            skCircle(sketch, "E95", {"center": v(0, 104.25) * mm, "radius": 5.8 * mm});
            skCircle(sketch, "E96", {"center": v(0, -104.25) * mm, "radius": 6 * mm});
            skSolve(sketch);
        }
        {
            var Q0;
            Q0=makeQuery(id+"F16.imprint","IMPRINT",FACE,{"disambiguationData":[TD([[makeQuery(id+"F16.imprint","IMPRINT",EDGE,{"derivedFrom":sQuery(id+"F16.wireOp",EDGE,"E80")}),1.0]])]});
            var Q1;
            Q1=makeQuery(id+"F16.imprint","IMPRINT",FACE,{"disambiguationData":[TD([[makeQuery(id+"F16.imprint","IMPRINT",EDGE,{"derivedFrom":sQuery(id+"F16.wireOp",EDGE,"E87.MirrorCS")}),-1.0]])]});
            var Q2;
            Q2=makeQuery(id+"F2.opExtrude","CAP_FACE",FACE,{"disambiguationData":[OSD([sQuery(id+"F0.wireOp",EDGE,"E12"),sQuery(id+"F0.wireOp",EDGE,"E13"),sQuery(id+"F0.wireOp",EDGE,"E14"),sQuery(id+"F0.wireOp",EDGE,"E15"),sQuery(id+"F0.wireOp",EDGE,"E17.filletArc"),sQuery(id+"F0.wireOp",EDGE,"E18.filletArc"),sQuery(id+"F0.wireOp",EDGE,"E19.filletArc"),sQuery(id+"F0.wireOp",EDGE,"E20.filletArc"),sQuery(id+"F0.wireOp",EDGE,"E25.0"),sQuery(id+"F0.wireOp",EDGE,"E25.1"),sQuery(id+"F0.wireOp",EDGE,"E25.2"),sQuery(id+"F0.wireOp",EDGE,"E25.3"),sQuery(id+"F0.wireOp",EDGE,"E25.4"),sQuery(id+"F0.wireOp",EDGE,"E25.5"),sQuery(id+"F0.wireOp",EDGE,"E25.6"),sQuery(id+"F0.wireOp",EDGE,"E25.7")])],"isStart":false});
            extrude(context, id + "F17", {"entities" : qUnion([Q0, Q1]), "operationType" : NewBodyOperationType.ADD, "endBound" : BoundingType.UP_TO_SURFACE, "endBoundEntityFace" : qUnion([Q2]), "depth" : 25 * mm});
        }
    });
